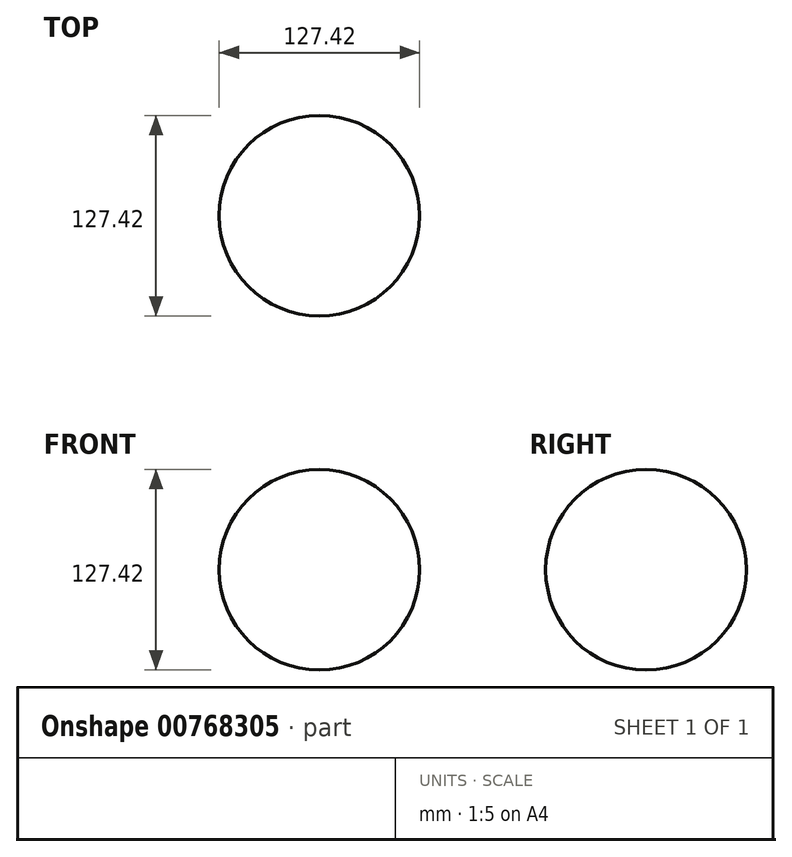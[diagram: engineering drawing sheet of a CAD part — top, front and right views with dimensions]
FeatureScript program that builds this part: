
annotation { "Feature Type Name" : "Feature", "Feature Type Description" : "" }
export const myFeature = defineFeature(function(context is Context, id is Id, definition is map)
    precondition{}
    {
        {
            var Q0;
            Q0=qCreatedBy(makeId("Front.planeOp"),FACE);
            var sketch = newSketch(context, id + "F0", { "sketchPlane" : qUnion([Q0])});
            skCircle(sketch, "E0", {"center": v(0, 0) * mm, "radius": 63.7 * mm});
            skLineSegment(sketch, "E1", {"start": v(0, 63.7) * mm, "end": v(0, -63.7) * mm});
            skSolve(sketch);
        }
        {
            var Q0;
            {var subQ0=sQuery(id+"F0.wireOp",EDGE,"E1");Q0=makeQuery(id+"F0.imprint","IMPRINT",FACE,{"disambiguationData":[TD([[makeQuery(id+"F0.imprint","IMPRINT",EDGE,{"derivedFrom":subQ0}),1.0]])]});}
            var Q1;
            Q1=sQuery(id+"F0.wireOp",EDGE,"E1");
            revolve(context, id + "F1", {"surfaceOperationType" : NewSurfaceOperationType.NEW, "entities" : qUnion([Q0]), "axis" : qUnion([Q1]), "revolveType" : RevolveType.FULL});
        }
    });
